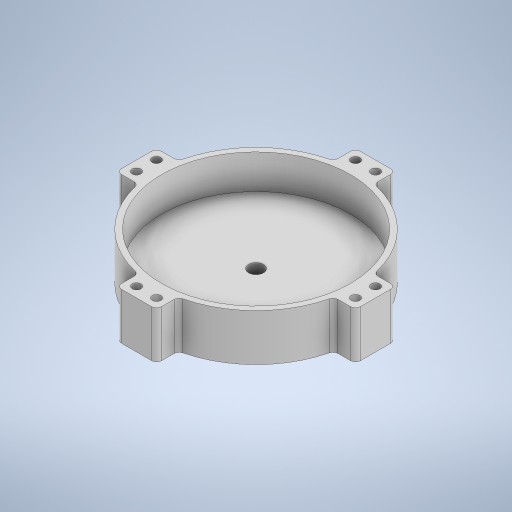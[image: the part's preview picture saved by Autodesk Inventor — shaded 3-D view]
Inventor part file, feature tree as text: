
AUTODESK INVENTOR PART (.ipt)
format: ipt  version: 2023 (Build 270158000, 158)  size: 494,592 bytes
history: native  units: in
note: dims shown in document units (in); Inventor stores cm internally (conversion verified against a paired STEP export)
features: extrude x3, sketch x3, fillet x2
ambient origin geometry x8: Origin, YZ Plane, XZ Plane, XY Plane, X Axis, Y Axis, Z Axis, Center Point
bodies: Solid1 (feature_tree)
feature tree (8):
  extrude  "Extrusion1"  Depth=0.3in
  extrude  "Extrusion2"  Depth=0.687in
  fillet  "Fillet1"  Radius=0.687in
  extrude  "Extrusion3"  Depth=0.1in
  fillet  "Fillet2"  Radius=0.5in
  sketch  "Sketch1"  dims[d0=4.0in d1=0.3in]
  sketch  "Sketch2"  dims[d2=0.25in d3=0.0in d4=3.78in d5=0.687in d6=0.0in]
  sketch  "Sketch3"  dims[d7=0.05in d8=0.4in d9=0.5in d10=0.5in d11=0.4in d12=0.4in d13=0.4in d14=0.5in d15=0.4in d16=0.4in d17=0.5in d18=0.4in d19=0.4in d20=0.2in d21=0.2in d22=0.2in d23=0.177in d24=0.177in d25=0.177in d26=0.177in d27=0.177in d28=0.177in d29=0.177in d30=0.177in d31=1.0in d32=0.0in d33=0.1in]
